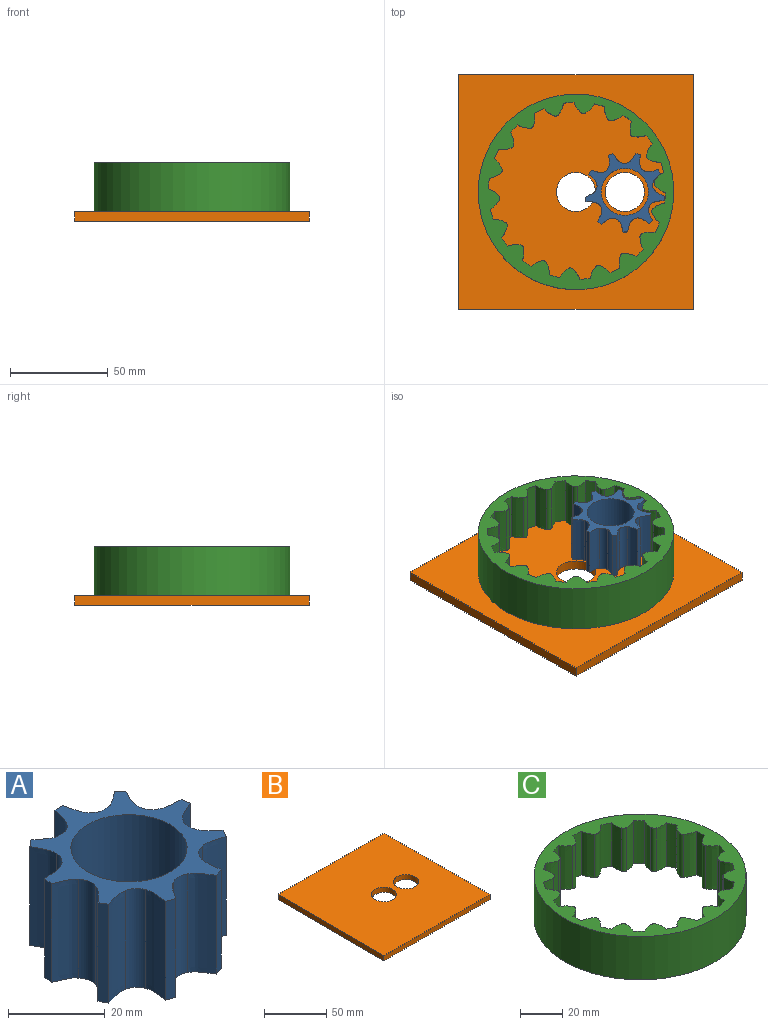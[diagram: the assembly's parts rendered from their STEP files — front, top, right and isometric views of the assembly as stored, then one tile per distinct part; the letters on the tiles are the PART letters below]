
ASSEMBLY  parts=3 mates=2
PART A: 39 faces, bbox 42.8x42.2x27 mm
  f0: extruded ~25x5.63mm, area 151.6mm2, adj f3,f4,f5,f31
  f1: extruded ~25x5.14mm, area 150.6mm2, adj f3,f4,f5,f30
  f2: cylinder r=12.02mm len=25mm, axis (0,0,-1), area 1888.6mm2, adj f3,f4
  f3: plane 42.75x42.15mm, normal (0,0,1), area 435mm2, adj f0,f1,f2,f5,f6,f7,f8,f9
  f4: plane 42.75x42.15mm, normal (0,0,-1), area 435mm2, adj f0,f1,f2,f5,f6,f7,f8,f9
  f5: plane 25x1.81mm, normal (0.63,0.77,0), area 58.4mm2, adj f0,f1,f3,f4
  f6: extruded ~25x5.63mm, area 151.6mm2, adj f3,f4,f8,f30
  f7: extruded ~25x5.6mm, area 150.6mm2, adj f3,f4,f8,f32
  f8: plane 25x2.34mm, normal (-0.01,1,0), area 58.4mm2, adj f3,f4,f6,f7
  f9: extruded ~25x5.19mm, area 151.6mm2, adj f3,f4,f11,f32
  f10: extruded ~25x5.58mm, area 150.6mm2, adj f3,f4,f11,f33
  f11: plane 25x1.77mm, normal (-0.65,0.76,0), area 58.4mm2, adj f3,f4,f9,f10
  f12: extruded ~25x5.9mm, area 151.6mm2, adj f3,f4,f14,f33
  f13: extruded ~25x5.17mm, area 150.6mm2, adj f3,f4,f14,f34
  f14: plane 25x2.3mm, normal (-0.99,0.16,0), area 58.4mm2, adj f3,f4,f12,f13
  f15: extruded ~25x4.59mm, area 151.6mm2, adj f3,f4,f29,f34
  f16: extruded ~25x5.9mm, area 151.6mm2, adj f3,f4,f18,f35
  f17: extruded ~25x4.54mm, area 150.6mm2, adj f3,f4,f18,f36
  f18: plane 25x2.04mm, normal (0.87,-0.49,0), area 58.4mm2, adj f3,f4,f16,f17
  f19: extruded ~25x5.19mm, area 151.6mm2, adj f3,f4,f21,f36
  f20: extruded ~25x5.87mm, area 150.6mm2, adj f3,f4,f21,f31
  f21: plane 25x2.29mm, normal (0.98,0.19,0), area 58.4mm2, adj f3,f4,f19,f20
  f22: extruded ~25x4.59mm, area 151.6mm2, adj f3,f4,f24,f37
  f23: extruded ~25x5.95mm, area 150.6mm2, adj f3,f4,f24,f35
  f24: plane 25x2.19mm, normal (0.35,-0.94,0), area 58.4mm2, adj f3,f4,f22,f23
  f25: extruded ~25x5.99mm, area 151.6mm2, adj f3,f4,f27,f38
  f26: extruded ~25x4.58mm, area 150.6mm2, adj f3,f4,f27,f37
  f27: plane 25x2.2mm, normal (-0.33,-0.94,0), area 58.4mm2, adj f3,f4,f25,f26
  f28: extruded ~25x5.86mm, area 150.6mm2, adj f3,f4,f29,f38
  f29: plane 25x2.01mm, normal (-0.86,-0.51,0), area 58.4mm2, adj f3,f4,f15,f28
  f30: cylinder r=4mm len=25mm, axis (0,0,-1), area 109.4mm2, adj f1,f3,f4,f6
  f31: cylinder r=4mm len=25mm, axis (0,0,-1), area 109.4mm2, adj f0,f3,f4,f20
  f32: cylinder r=4mm len=25mm, axis (0,0,-1), area 109.4mm2, adj f3,f4,f7,f9
  f33: cylinder r=4mm len=25mm, axis (0,0,-1), area 109.4mm2, adj f3,f4,f10,f12
  f34: cylinder r=4mm len=25mm, axis (0,0,-1), area 109.4mm2, adj f3,f4,f13,f15
  f35: cylinder r=4mm len=25mm, axis (0,0,-1), area 109.4mm2, adj f3,f4,f16,f23
  f36: cylinder r=4mm len=25mm, axis (0,0,-1), area 109.4mm2, adj f3,f4,f17,f19
  f37: cylinder r=4mm len=25mm, axis (0,0,-1), area 109.4mm2, adj f3,f4,f22,f26
  f38: cylinder r=4mm len=25mm, axis (0,0,-1), area 109.4mm2, adj f3,f4,f25,f28
PART B: 8 faces, bbox 120x120x5 mm
  f0: plane 120x5mm, normal (1,0,0), area 600mm2, adj f1,f4,f6,f7
  f1: plane 120x5mm, normal (0,1,0), area 600mm2, adj f0,f2,f6,f7
  f2: plane 120x5mm, normal (-1,0,0), area 600mm2, adj f1,f4,f6,f7
  f3: cylinder r=10mm len=20mm, axis (0,0,1), area 314.2mm2, adj f6,f7
  f4: plane 120x5mm, normal (0,-1,0), area 600mm2, adj f0,f2,f6,f7
  f5: cylinder r=10mm len=20mm, axis (0,0,1), area 314.2mm2, adj f6,f7
  f6: plane 120x120mm, normal (0,0,-1), area 13771.7mm2, adj f0,f1,f2,f3,f4,f5
  f7: plane 120x120mm, normal (0,0,1), area 13771.7mm2, adj f0,f1,f2,f3,f4,f5
PART C: 75 faces, bbox 100x100x25 mm
  f0: extruded ~25x6.21mm, area 157.1mm2, adj f2,f3,f4,f73
  f1: extruded ~25x5.97mm, area 157.1mm2, adj f2,f3,f4,f5
  f2: plane 100x100mm, normal (0,0,1), area 2100.2mm2, adj f0,f1,f4,f5,f6,f7,f8,f9
  f3: plane 100x100mm, normal (0,0,-1), area 2100.2mm2, adj f0,f1,f4,f5,f6,f7,f8,f9
  f4: cylinder r=2mm len=25mm, axis (0,0,-1), area 70.9mm2, adj f0,f1,f2,f3
  f5: cylinder r=45.24mm len=25mm, axis (0,0,-1), area 135.3mm2, adj f1,f2,f3,f6
  f6: extruded ~25x5.97mm, area 157.1mm2, adj f2,f3,f5,f8
  f7: extruded ~25x6.21mm, area 157.1mm2, adj f2,f3,f8,f9
  f8: cylinder r=2mm len=25mm, axis (0,0,-1), area 70.9mm2, adj f2,f3,f6,f7
  f9: cylinder r=45.24mm len=25mm, axis (0,0,-1), area 135.3mm2, adj f2,f3,f7,f10
  f10: extruded ~25x5mm, area 157.1mm2, adj f2,f3,f9,f12
  f11: extruded ~25x5.7mm, area 157.1mm2, adj f2,f3,f12,f13
  f12: cylinder r=2mm len=25mm, axis (0,0,-1), area 70.9mm2, adj f2,f3,f10,f11
  f13: cylinder r=45.24mm len=25mm, axis (0,0,-1), area 135.3mm2, adj f2,f3,f11,f14
  f14: extruded ~25x5.19mm, area 157.1mm2, adj f2,f3,f13,f16
  f15: extruded ~25x4.51mm, area 157.1mm2, adj f2,f3,f16,f17
  f16: cylinder r=2mm len=25mm, axis (0,0,-1), area 70.9mm2, adj f2,f3,f14,f15
  f17: cylinder r=45.24mm len=25mm, axis (0,0,-1), area 135.3mm2, adj f2,f3,f15,f18
  f18: extruded ~25x6.05mm, area 157.1mm2, adj f2,f3,f17,f20
  f19: extruded ~25x5.57mm, area 157.1mm2, adj f2,f3,f20,f21
  f20: cylinder r=2mm len=25mm, axis (0,0,-1), area 70.9mm2, adj f2,f3,f18,f19
  f21: cylinder r=45.24mm len=25mm, axis (0,0,-1), area 135.3mm2, adj f2,f3,f19,f22
  f22: extruded ~25x6.18mm, area 157.1mm2, adj f2,f3,f21,f24
  f23: extruded ~25x6.18mm, area 157.1mm2, adj f2,f3,f24,f25
  f24: cylinder r=2mm len=25mm, axis (0,0,-1), area 70.9mm2, adj f2,f3,f22,f23
  f25: cylinder r=45.24mm len=25mm, axis (0,0,-1), area 135.3mm2, adj f2,f3,f23,f26
  f26: extruded ~25x5.57mm, area 157.1mm2, adj f2,f3,f25,f28
  f27: extruded ~25x6.05mm, area 157.1mm2, adj f2,f3,f28,f29
  f28: cylinder r=2mm len=25mm, axis (0,0,-1), area 70.9mm2, adj f2,f3,f26,f27
  f29: cylinder r=45.24mm len=25mm, axis (0,0,-1), area 135.3mm2, adj f2,f3,f27,f30
  f30: extruded ~25x4.51mm, area 157.1mm2, adj f2,f3,f29,f32
  f31: extruded ~25x5.19mm, area 157.1mm2, adj f2,f3,f32,f33
  f32: cylinder r=2mm len=25mm, axis (0,0,-1), area 70.9mm2, adj f2,f3,f30,f31
  f33: cylinder r=45.24mm len=25mm, axis (0,0,-1), area 135.3mm2, adj f2,f3,f31,f34
  f34: extruded ~25x5.7mm, area 157.1mm2, adj f2,f3,f33,f36
  f35: extruded ~25x5mm, area 157.1mm2, adj f2,f3,f36,f37
  f36: cylinder r=2mm len=25mm, axis (0,0,-1), area 70.9mm2, adj f2,f3,f34,f35
  f37: cylinder r=45.24mm len=25mm, axis (0,0,-1), area 135.3mm2, adj f2,f3,f35,f38
  f38: extruded ~25x6.21mm, area 157.1mm2, adj f2,f3,f37,f40
  f39: extruded ~25x5.97mm, area 157.1mm2, adj f2,f3,f40,f41
  f40: cylinder r=2mm len=25mm, axis (0,0,-1), area 70.9mm2, adj f2,f3,f38,f39
  f41: cylinder r=45.24mm len=25mm, axis (0,0,-1), area 135.3mm2, adj f2,f3,f39,f42
  f42: extruded ~25x5.97mm, area 157.1mm2, adj f2,f3,f41,f44
  f43: extruded ~25x6.21mm, area 157.1mm2, adj f2,f3,f44,f45
  f44: cylinder r=2mm len=25mm, axis (0,0,-1), area 70.9mm2, adj f2,f3,f42,f43
  f45: cylinder r=45.24mm len=25mm, axis (0,0,-1), area 135.3mm2, adj f2,f3,f43,f46
  f46: extruded ~25x5mm, area 157.1mm2, adj f2,f3,f45,f48
  f47: extruded ~25x5.7mm, area 157.1mm2, adj f2,f3,f48,f49
  f48: cylinder r=2mm len=25mm, axis (0,0,-1), area 70.9mm2, adj f2,f3,f46,f47
  f49: cylinder r=45.24mm len=25mm, axis (0,0,-1), area 135.3mm2, adj f2,f3,f47,f50
  f50: extruded ~25x5.19mm, area 157.1mm2, adj f2,f3,f49,f52
  f51: extruded ~25x4.51mm, area 157.1mm2, adj f2,f3,f52,f53
  f52: cylinder r=2mm len=25mm, axis (0,0,-1), area 70.9mm2, adj f2,f3,f50,f51
  f53: cylinder r=45.24mm len=25mm, axis (0,0,-1), area 135.3mm2, adj f2,f3,f51,f54
  f54: extruded ~25x6.05mm, area 157.1mm2, adj f2,f3,f53,f56
  f55: extruded ~25x5.57mm, area 157.1mm2, adj f2,f3,f56,f57
  f56: cylinder r=2mm len=25mm, axis (0,0,-1), area 70.9mm2, adj f2,f3,f54,f55
  f57: cylinder r=45.24mm len=25mm, axis (0,0,-1), area 135.3mm2, adj f2,f3,f55,f58
  f58: extruded ~25x6.18mm, area 157.1mm2, adj f2,f3,f57,f60
  f59: extruded ~25x6.18mm, area 157.1mm2, adj f2,f3,f60,f61
  f60: cylinder r=2mm len=25mm, axis (0,0,-1), area 70.9mm2, adj f2,f3,f58,f59
  f61: cylinder r=45.24mm len=25mm, axis (0,0,-1), area 135.3mm2, adj f2,f3,f59,f62
  f62: extruded ~25x5.57mm, area 157.1mm2, adj f2,f3,f61,f64
  f63: extruded ~25x6.05mm, area 157.1mm2, adj f2,f3,f64,f65
  f64: cylinder r=2mm len=25mm, axis (0,0,-1), area 70.9mm2, adj f2,f3,f62,f63
  f65: cylinder r=45.24mm len=25mm, axis (0,0,-1), area 135.3mm2, adj f2,f3,f63,f66
  f66: extruded ~25x4.51mm, area 157.1mm2, adj f2,f3,f65,f68
  f67: extruded ~25x5.19mm, area 157.1mm2, adj f2,f3,f68,f69
  f68: cylinder r=2mm len=25mm, axis (0,0,-1), area 70.9mm2, adj f2,f3,f66,f67
  f69: cylinder r=45.24mm len=25mm, axis (0,0,-1), area 135.3mm2, adj f2,f3,f67,f70
  f70: extruded ~25x5.7mm, area 157.1mm2, adj f2,f3,f69,f72
  f71: extruded ~25x5mm, area 157.1mm2, adj f2,f3,f72,f73
  f72: cylinder r=2mm len=25mm, axis (0,0,-1), area 70.9mm2, adj f2,f3,f70,f71
  f73: cylinder r=45.24mm len=25mm, axis (0,0,-1), area 135.3mm2, adj f0,f2,f3,f71
  f74: cylinder r=50mm len=100mm, axis (0,0,-1), area 7854mm2, adj f2,f3
PLACE A rot(axis=(0,0,1),100.7deg) t=(25,0,5)mm
PLACE B t=(25,0,5)mm
PLACE C rot(axis=(0,0,-1),129.7deg) t=(-15.47,-18.66,5)mm
MATE revolute A.f2 <-> B.f5  axis (0,0,-1) through (25,0,5)mm
MATE revolute C.f74 <-> B.f3  axis (0,0,-1) through (0,0,5)mm
